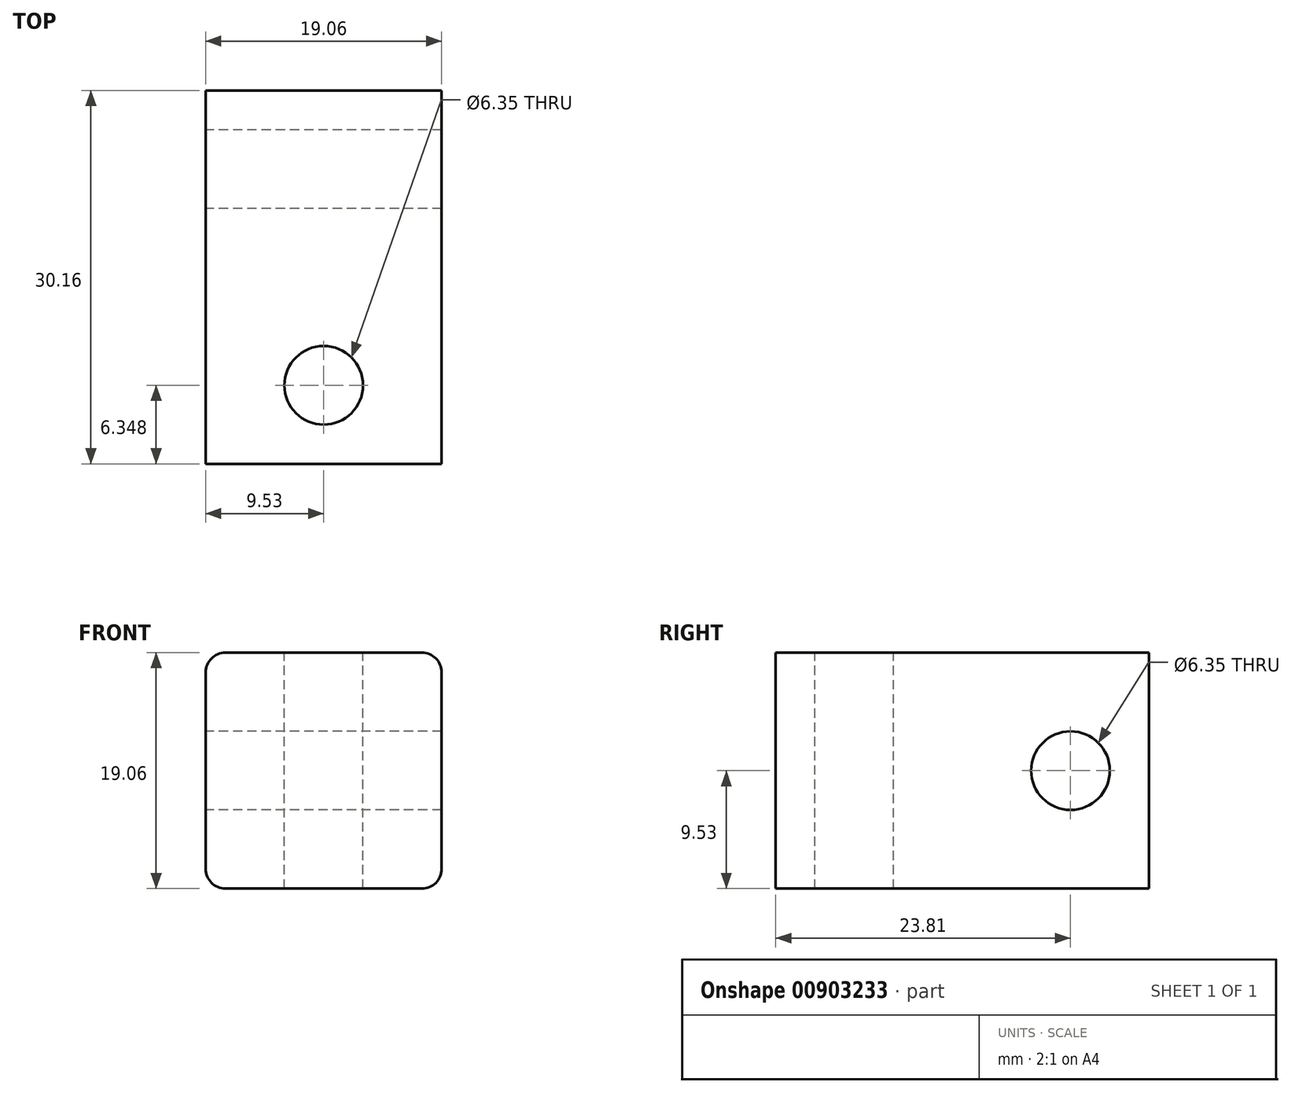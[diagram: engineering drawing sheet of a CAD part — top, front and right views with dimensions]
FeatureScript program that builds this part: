
annotation { "Feature Type Name" : "Feature", "Feature Type Description" : "" }
export const myFeature = defineFeature(function(context is Context, id is Id, definition is map)
    precondition{}
    {
        {
            var Q0;
            Q0=qCreatedBy(makeId("Front.planeOp"),FACE);
            var sketch = newSketch(context, id + "F0", { "sketchPlane" : qUnion([Q0])});
            skLineSegment(sketch, "E0.bottom", {"start": v(7.94, 9.53) * mm, "end": v(-7.94, 9.53) * mm});
            skLineSegment(sketch, "E0.top", {"start": v(7.94, -9.52) * mm, "end": v(-7.94, -9.52) * mm});
            skLineSegment(sketch, "E0.left", {"start": v(9.53, 7.94) * mm, "end": v(9.53, -7.94) * mm});
            skLineSegment(sketch, "E0.right", {"start": v(-9.53, 7.94) * mm, "end": v(-9.53, -7.94) * mm});
            skPoint(sketch, "E0.middle", {"position": v(0, 0) * mm});
            skPoint(sketch, "E1.visualSharp", {"position": v(-9.53, 9.53) * mm});
            skArc(sketch, "E1.filletArc", {"start": v(-7.94, 9.53) * mm, "mid": v(-9.06, 9.06) * mm, "end": v(-9.53, 7.94) * mm});
            skPoint(sketch, "E2.visualSharp", {"position": v(-9.53, -9.52) * mm});
            skArc(sketch, "E2.filletArc", {"start": v(-9.53, -7.94) * mm, "mid": v(-9.06, -9.06) * mm, "end": v(-7.94, -9.52) * mm});
            skPoint(sketch, "E3.visualSharp", {"position": v(9.53, -9.52) * mm});
            skArc(sketch, "E3.filletArc", {"start": v(7.94, -9.52) * mm, "mid": v(9.06, -9.06) * mm, "end": v(9.53, -7.94) * mm});
            skPoint(sketch, "E4.visualSharp", {"position": v(9.53, 9.53) * mm});
            skArc(sketch, "E4.filletArc", {"start": v(9.53, 7.94) * mm, "mid": v(9.06, 9.06) * mm, "end": v(7.94, 9.53) * mm});
            skSolve(sketch);
        }
        {
            var Q0;
            Q0=makeQuery(id+"F0.imprint","IMPRINT",FACE,{"disambiguationData":[TD([[makeQuery(id+"F0.imprint","IMPRINT",EDGE,{"derivedFrom":sQuery(id+"F0.wireOp",EDGE,"E0.bottom")}),1.0]])]});
            extrude(context, id + "F1", {"entities" : qUnion([Q0]), "depth" : 30.16 * mm, "offsetDistance" : 25.4 * mm});
        }
        {
            var Q0;
            Q0=makeQuery(id+"F1.opExtrude","SWEPT_FACE",FACE,{"disambiguationData":[OSD([sQuery(id+"F0.wireOp",EDGE,"E0.bottom")])]});
            var sketch = newSketch(context, id + "F2", { "sketchPlane" : qUnion([Q0])});
            skCircle(sketch, "E5", {"center": v(0, -23.81) * mm, "radius": 3.17 * mm});
            skSolve(sketch);
        }
        {
            var Q0;
            Q0=makeQuery(id+"F2.imprint","IMPRINT",FACE,{"disambiguationData":[TD([[makeQuery(id+"F2.imprint","IMPRINT",EDGE,{"derivedFrom":sQuery(id+"F2.wireOp",EDGE,"E5")}),1.0]])]});
            extrude(context, id + "F3", {"entities" : qUnion([Q0]), "operationType" : NewBodyOperationType.REMOVE, "endBound" : BoundingType.THROUGH_ALL, "oppositeDirection" : true, "depth" : 25.4 * mm, "offsetDistance" : 25.4 * mm});
        }
        {
            var Q0;
            Q0=makeQuery(id+"F1.opExtrude","SWEPT_FACE",FACE,{"disambiguationData":[OSD([sQuery(id+"F0.wireOp",EDGE,"E0.right")])]});
            var sketch = newSketch(context, id + "F4", { "sketchPlane" : qUnion([Q0])});
            skCircle(sketch, "E6", {"center": v(6.35, 0) * mm, "radius": 3.18 * mm});
            skSolve(sketch);
        }
        {
            var Q0;
            Q0=makeQuery(id+"F4.imprint","IMPRINT",FACE,{"disambiguationData":[TD([[makeQuery(id+"F4.imprint","IMPRINT",EDGE,{"derivedFrom":sQuery(id+"F4.wireOp",EDGE,"E6")}),1.0]])]});
            extrude(context, id + "F5", {"entities" : qUnion([Q0]), "operationType" : NewBodyOperationType.REMOVE, "endBound" : BoundingType.THROUGH_ALL, "oppositeDirection" : true, "depth" : 25.4 * mm, "offsetDistance" : 25.4 * mm});
        }
    });
